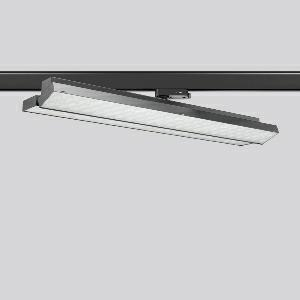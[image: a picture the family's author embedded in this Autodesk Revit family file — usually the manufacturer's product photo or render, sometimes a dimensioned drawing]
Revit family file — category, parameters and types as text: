
# Revit family: tx-move_742163_003_2_76_86ac
name_source: partatom
category: Lighting Fixtures
units: mm (PartAtom-declared; Revit-internal decimal feet)

## family parameters
Cut with Voids When Loaded = No
Host = Face
Light Source = No
Part Type = Normal
Room Calculation Point = No
Round Connector Dimension = Use Diameter
Shared = No

## types (1)
- MultiLumen 1 (1 x LED Modul 927, 1975 lm, 2700)
    Apparent Load = 38 VA
    CIE Flux Codes = 65 90 98 100 100
    Color Rendering = 92
    Color Temperature = 2700
    Default Elevation = 1800 mm
    Description = Series: TX-MOVE
Multifunctional surface-mounted spotlight for area lighting. Very flat design. Housing: sheet steel, powder-coated. Rotation range: 356°. Swivel range: 90°. Consistent alignment possible with visible tilt scale. High-efficiency LED units with optimum light control thanks to clear plastic (PC) lens optics. Spezielle Mikrostrukturen reduzieren Gelbsaum. Asymmetrical light distribution. Best colour rendering with CRI >90 for fresh products and coloured textiles. With adapter for RZB 3-circuit DALI tracks. Suitable for Track on ceiling. MultiLumen: Luminous flux adjustable in 3 steps. Factory setting is the highest luminous flux. Environmentally friendly and resource-saving due to replaceable and recyclable components. 
Colour: deep black, matt (RAL 9005)
Length: 570 mm
Width: 119 mm
Height: 88 mm
Lamp: LED
Socket: without socket
Colour temperature: 2700K
Colour rendering index (CRI): 90
System power: 38 W
Rated luminous flux: 3950 lm
Luminous efficiency: 104 lm/W
System power 2: 51 W
Rated luminous flux 2: 5150 lm
Luminous efficiency 2: 101 lm/W
System power 3: 62 W
Rated luminous flux 3: 6150 lm
Luminous efficiency 3: 99 lm/W
Control gear: Dimmable EVG, DALI
Protection class: I
Type of protection: IP 20
    Height = 75 mm
    Lamp = 1 x LED Modul 927
    Lamp Light Flux = 1975 lm
    Lamp count = 1
    Length = 569 mm
    Lifetime = 50000 h
    Luminous efficacy = 104 lm/W
    Manufacturer = RZB
    ModVariant = No
    Model = 742163.003.2.76
    Mounting Place = Ceiling
    Mounting Type = Surface mounted
    Number of Poles = 1
    OnlyDefault = Yes
    Power Factor = 1
    Product Name = TX-MOVE
    Product group = Track mounted projectors
    ProductGroupID = 301
    Protection Class = Protection class I
    Protection Degree = IP 20
    RLX_Detail_Level = 1
    RLX_Emergency_Light_Flux = 0 lm
    RLX_Emergency_Type = 0
    RLX_Emergency_Type_DB = No
    RlxData = <blob elided: 57513 chars, md5=9f1252a7>
    Socket = socket
    Standby Power = 0 W
    System Light Flux = 3950 lm
    System Power = 38 W
    Type Comments = MultiLumen 1
    Type Image = 742162.003.jpg
    URL = http://relux.com
    VarID = multilumen_1
    Voltage = 0 V
    Weight = 0.00 kg
    Width = 119 mm

## geometry (parser evidence)
native form markers: Blend x4, Sweep x16
no freeform markers — native parametric forms only
